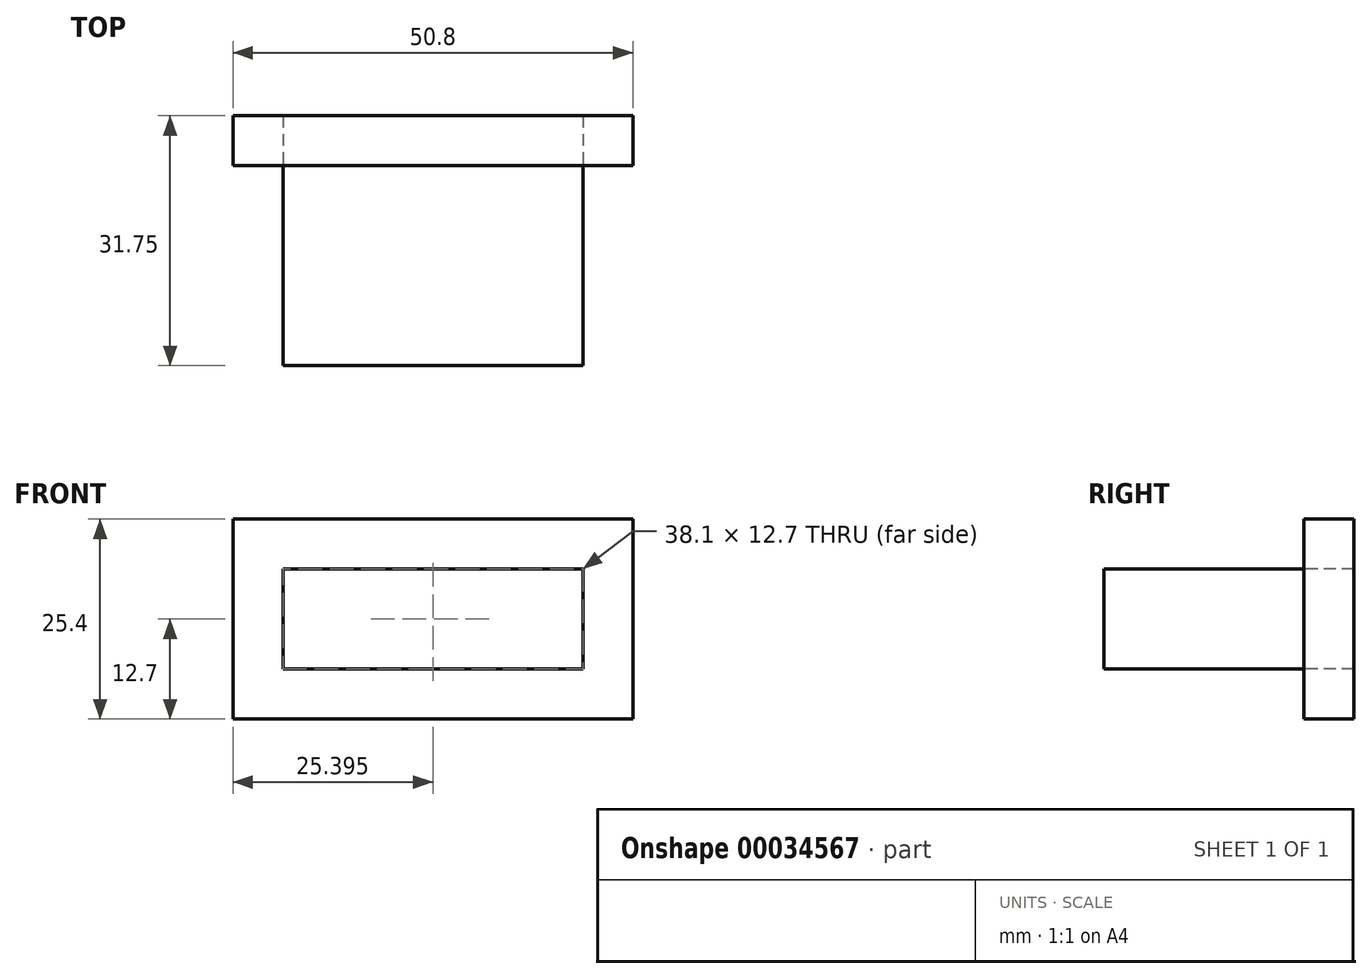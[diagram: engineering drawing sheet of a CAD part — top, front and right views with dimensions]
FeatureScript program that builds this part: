
annotation { "Feature Type Name" : "Feature", "Feature Type Description" : "" }
export const myFeature = defineFeature(function(context is Context, id is Id, definition is map)
    precondition{}
    {
        {
            var Q0;
            Q0=qCreatedBy(makeId("Front.planeOp"),FACE);
            var sketch = newSketch(context, id + "F0", { "sketchPlane" : qUnion([Q0])});
            skLineSegment(sketch, "E0.bottom", {"start": v(-20.46, 3.81) * mm, "end": v(17.64, 3.81) * mm});
            skLineSegment(sketch, "E0.top", {"start": v(-20.46, -8.89) * mm, "end": v(17.64, -8.89) * mm});
            skLineSegment(sketch, "E0.left", {"start": v(-20.46, 3.81) * mm, "end": v(-20.46, -8.89) * mm});
            skLineSegment(sketch, "E0.right", {"start": v(17.64, 3.81) * mm, "end": v(17.64, -8.89) * mm});
            skSolve(sketch);
        }
        {
            var Q0;
            Q0=qSketchRegion(id+"F0",true);
            extrude(context, id + "F1", {"entities" : qUnion([Q0]), "oppositeDirection" : true, "depth" : 25.4 * mm});
        }
        {
            var Q0;
            Q0=makeQuery(id+"F1.opExtrude","CAP_FACE",FACE,{"disambiguationData":[OSD([sQuery(id+"F0.wireOp",EDGE,"E0.bottom"),sQuery(id+"F0.wireOp",EDGE,"E0.top"),sQuery(id+"F0.wireOp",EDGE,"E0.left"),sQuery(id+"F0.wireOp",EDGE,"E0.right")])],"isStart":false});
            var sketch = newSketch(context, id + "F2", { "sketchPlane" : qUnion([Q0])});
            skLineSegment(sketch, "E1.bottom", {"start": v(-23.99, 10.16) * mm, "end": v(26.81, 10.16) * mm});
            skLineSegment(sketch, "E1.top", {"start": v(-23.99, -15.24) * mm, "end": v(26.81, -15.24) * mm});
            skLineSegment(sketch, "E1.left", {"start": v(-23.99, 10.16) * mm, "end": v(-23.99, -15.24) * mm});
            skLineSegment(sketch, "E1.right", {"start": v(26.81, 10.16) * mm, "end": v(26.81, -15.24) * mm});
            skSolve(sketch);
        }
        {
            var Q0;
            Q0=makeQuery(id+"F2.imprint","IMPRINT",FACE,{"disambiguationData":[TD([[makeQuery(id+"F2.imprint","IMPRINT",EDGE,{"derivedFrom":sQuery(id+"F2.wireOp",EDGE,"E1.bottom")}),-1.0]])]});
            extrude(context, id + "F3", {"entities" : qUnion([Q0]), "depth" : 6.35 * mm});
        }
    });
